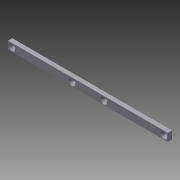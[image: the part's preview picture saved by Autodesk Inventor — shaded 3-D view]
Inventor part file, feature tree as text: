
AUTODESK INVENTOR PART (.ipt)
format: ipt  version: 2012 (Build 160160000, 160)  size: 92,672 bytes
history: native  units: in
note: dims shown in document units (in); Inventor stores cm internally (conversion verified against a paired STEP export)
features: reference x4, sketch x2, extrude x1, hole x1
ambient origin geometry x8: Origin, YZ Plane, XZ Plane, XY Plane, X Axis, Y Axis, Z Axis, Center Point
bodies: Solid1 (feature_tree)
feature tree (8):
  extrude  "Extrusion1"  Depth=0.375in
  hole  "Hole1"  [1 undecoded]
  sketch  "Sketch1"  dims[d0=7.7in d1=0.375in]
  sketch  "Sketch2"  dims[d2=0.2in d3=0.0in d4=0.177in d5=0.75in d6=0.332in d7=0.25in d8=0.5635in d9=1.0in d10=0.8108in]
  reference  "Reference1"
  reference  "Reference2"
  reference  "Reference3"
  reference  "Reference4"
note: 1 required parameter value undecoded (feature->parameter linkage not recoverable at this tier; creation-order binding heuristic only, values carry confidence <= 0.55)
